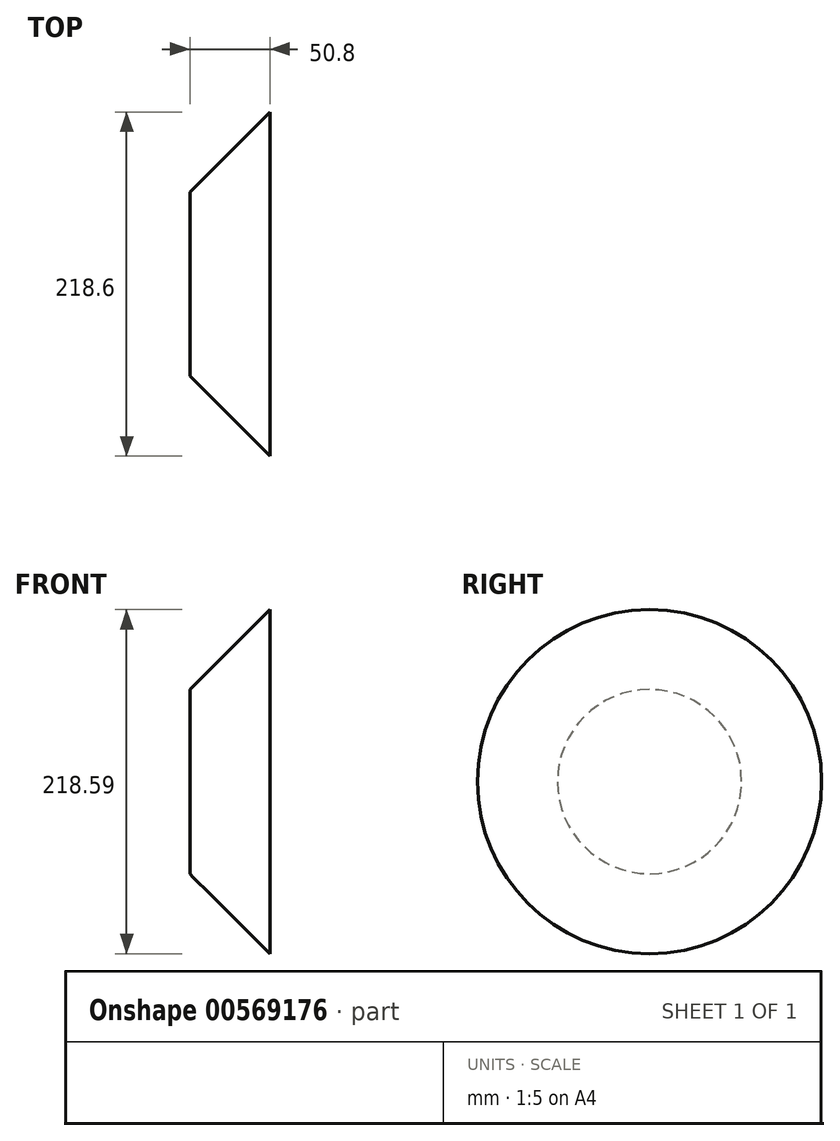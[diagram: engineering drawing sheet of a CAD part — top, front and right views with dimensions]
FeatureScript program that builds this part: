
annotation { "Feature Type Name" : "Feature", "Feature Type Description" : "" }
export const myFeature = defineFeature(function(context is Context, id is Id, definition is map)
    precondition{}
    {
        {
            var Q0;
            Q0=qCreatedBy(makeId("Right.planeOp"),FACE);
            var sketch = newSketch(context, id + "F0", { "sketchPlane" : qUnion([Q0])});
            skCircle(sketch, "E0", {"center": v(72.25, 25.47) * mm, "radius": 58.5 * mm});
            skPoint(sketch, "E0.first.point", {"position": v(46.04, 77.76) * mm});
            skPoint(sketch, "E0.second.point", {"position": v(30.5, 66.43) * mm});
            skPoint(sketch, "E0.third.point", {"position": v(61.68, 83) * mm});
            skSolve(sketch);
        }
        {
            var Q0;
            Q0=makeQuery(id+"F0.imprint","IMPRINT",FACE,{"disambiguationData":[TD([[makeQuery(id+"F0.imprint","IMPRINT",EDGE,{"derivedFrom":sQuery(id+"F0.wireOp",EDGE,"E0")}),1.0]])]});
            extrude(context, id + "F1", {"entities" : qUnion([Q0]), "depth" : 50.8 * mm, "offsetDistance" : 25.4 * mm, "hasDraft" : true, "draftAngle" : 45 * degree});
        }
    });
